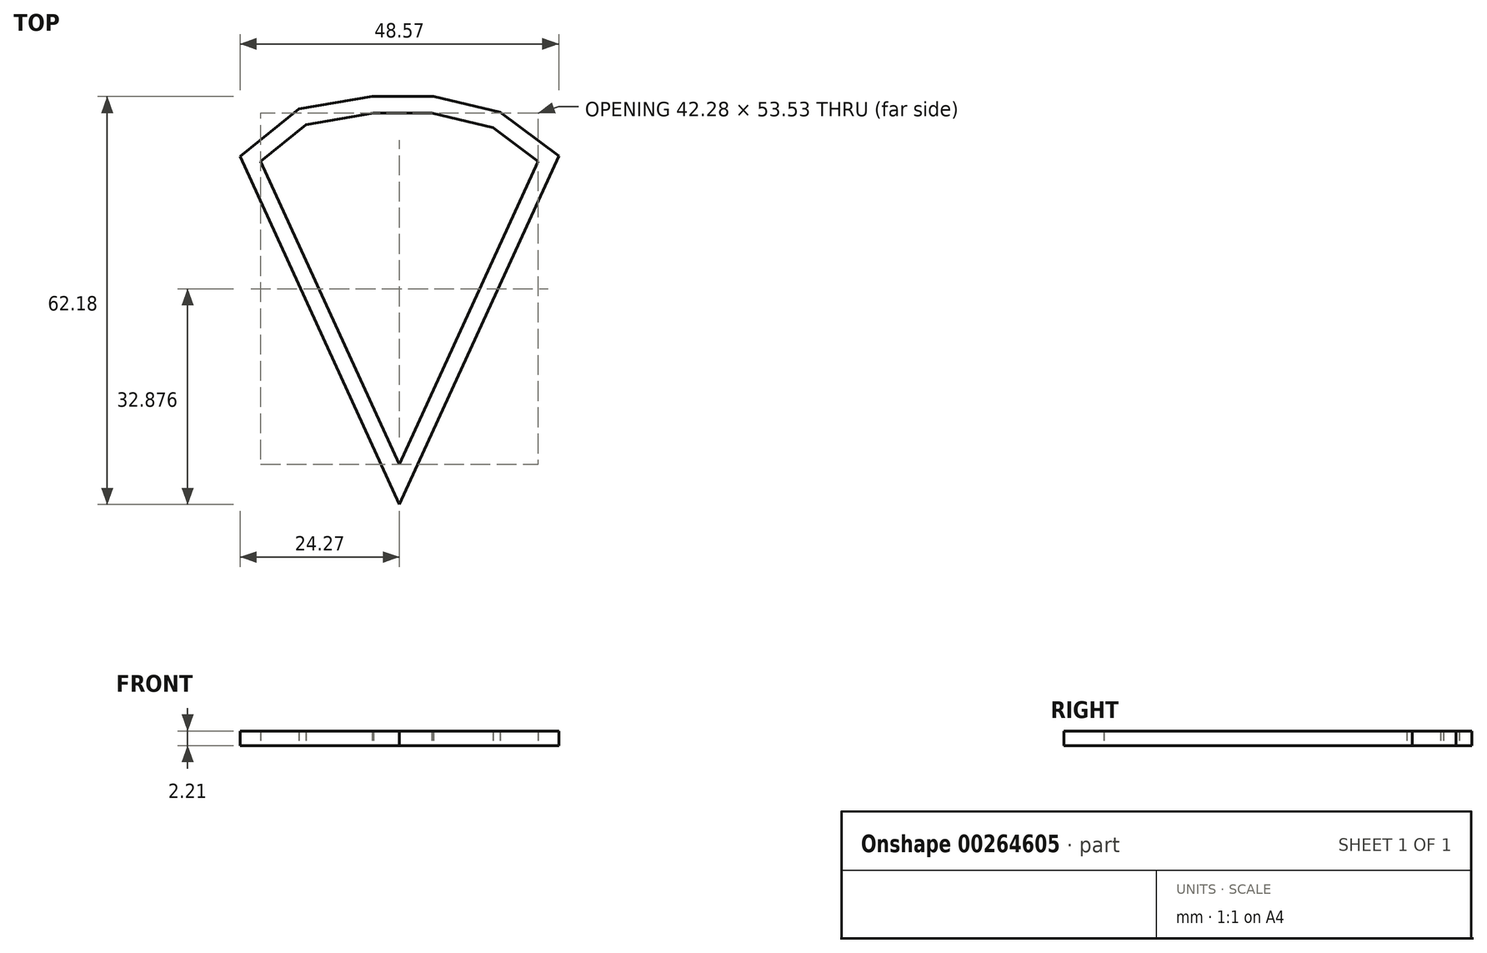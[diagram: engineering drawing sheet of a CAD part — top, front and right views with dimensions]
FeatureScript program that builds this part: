
annotation { "Feature Type Name" : "Feature", "Feature Type Description" : "" }
export const myFeature = defineFeature(function(context is Context, id is Id, definition is map)
    precondition{}
    {
        {
            var Q0;
            Q0=qCreatedBy(makeId("Top.planeOp"),FACE);
            var sketch = newSketch(context, id + "F0", { "sketchPlane" : qUnion([Q0])});
            skLineSegment(sketch, "E0", {"start": v(67.12, -28.5) * mm, "end": v(88.26, -74.7) * mm});
            skLineSegment(sketch, "E1", {"start": v(109.4, -28.5) * mm, "end": v(88.26, -74.7) * mm});
            skLineSegment(sketch, "E2", {"start": v(88.26, -74.7) * mm, "end": v(95.01, -29.47) * mm});
            skLineSegment(sketch, "E3", {"start": v(88.26, -74.7) * mm, "end": v(81.55, -29.47) * mm});
            skLineSegment(sketch, "E4", {"start": v(81.55, -29.47) * mm, "end": v(95.01, -29.47) * mm});
            skLineSegment(sketch, "E5", {"start": v(95.01, -29.47) * mm, "end": v(109.4, -28.5) * mm});
            skLineSegment(sketch, "E6", {"start": v(81.55, -29.47) * mm, "end": v(67.12, -28.5) * mm});
            skLineSegment(sketch, "E7", {"start": v(81.55, -29.47) * mm, "end": v(84.01, -25.02) * mm});
            skLineSegment(sketch, "E8", {"start": v(84.01, -25.02) * mm, "end": v(92.55, -25.02) * mm});
            skLineSegment(sketch, "E9", {"start": v(92.55, -25.02) * mm, "end": v(95.01, -29.47) * mm});
            skLineSegment(sketch, "E10", {"start": v(84.01, -25.02) * mm, "end": v(74.05, -22.92) * mm});
            skLineSegment(sketch, "E11", {"start": v(74.05, -22.92) * mm, "end": v(67.12, -28.5) * mm});
            skLineSegment(sketch, "E12", {"start": v(102.52, -23.34) * mm, "end": v(109.4, -28.5) * mm});
            skLineSegment(sketch, "E13", {"start": v(92.55, -25.02) * mm, "end": v(102.52, -23.34) * mm});
            skLineSegment(sketch, "E14", {"start": v(93.2, -21.16) * mm, "end": v(84.33, -21.16) * mm});
            skLineSegment(sketch, "E15", {"start": v(93.2, -21.16) * mm, "end": v(102.52, -23.34) * mm});
            skLineSegment(sketch, "E16", {"start": v(84.33, -21.16) * mm, "end": v(74.05, -22.92) * mm});
            skLineSegment(sketch, "E17.0", {"start": v(84.12, -18.62) * mm, "end": v(72.98, -20.53) * mm});
            skLineSegment(sketch, "E17.1", {"start": v(93.49, -18.62) * mm, "end": v(84.12, -18.62) * mm});
            skLineSegment(sketch, "E17.2", {"start": v(63.99, -27.76) * mm, "end": v(88.26, -80.8) * mm});
            skLineSegment(sketch, "E17.3", {"start": v(112.56, -27.7) * mm, "end": v(88.26, -80.8) * mm});
            skLineSegment(sketch, "E17.4", {"start": v(103.61, -21) * mm, "end": v(112.56, -27.7) * mm});
            skLineSegment(sketch, "E17.5", {"start": v(72.98, -20.53) * mm, "end": v(63.99, -27.76) * mm});
            skLineSegment(sketch, "E17.6", {"start": v(93.49, -18.62) * mm, "end": v(103.61, -21) * mm});
            skSolve(sketch);
        }
        {
            var Q0;
            Q0 = qSketchRegion(id + "F0", true);
            extrude(context, id + "F1", {"entities" : qUnion([Q0]), "depth" : 2.2 * mm});
        }
    });
